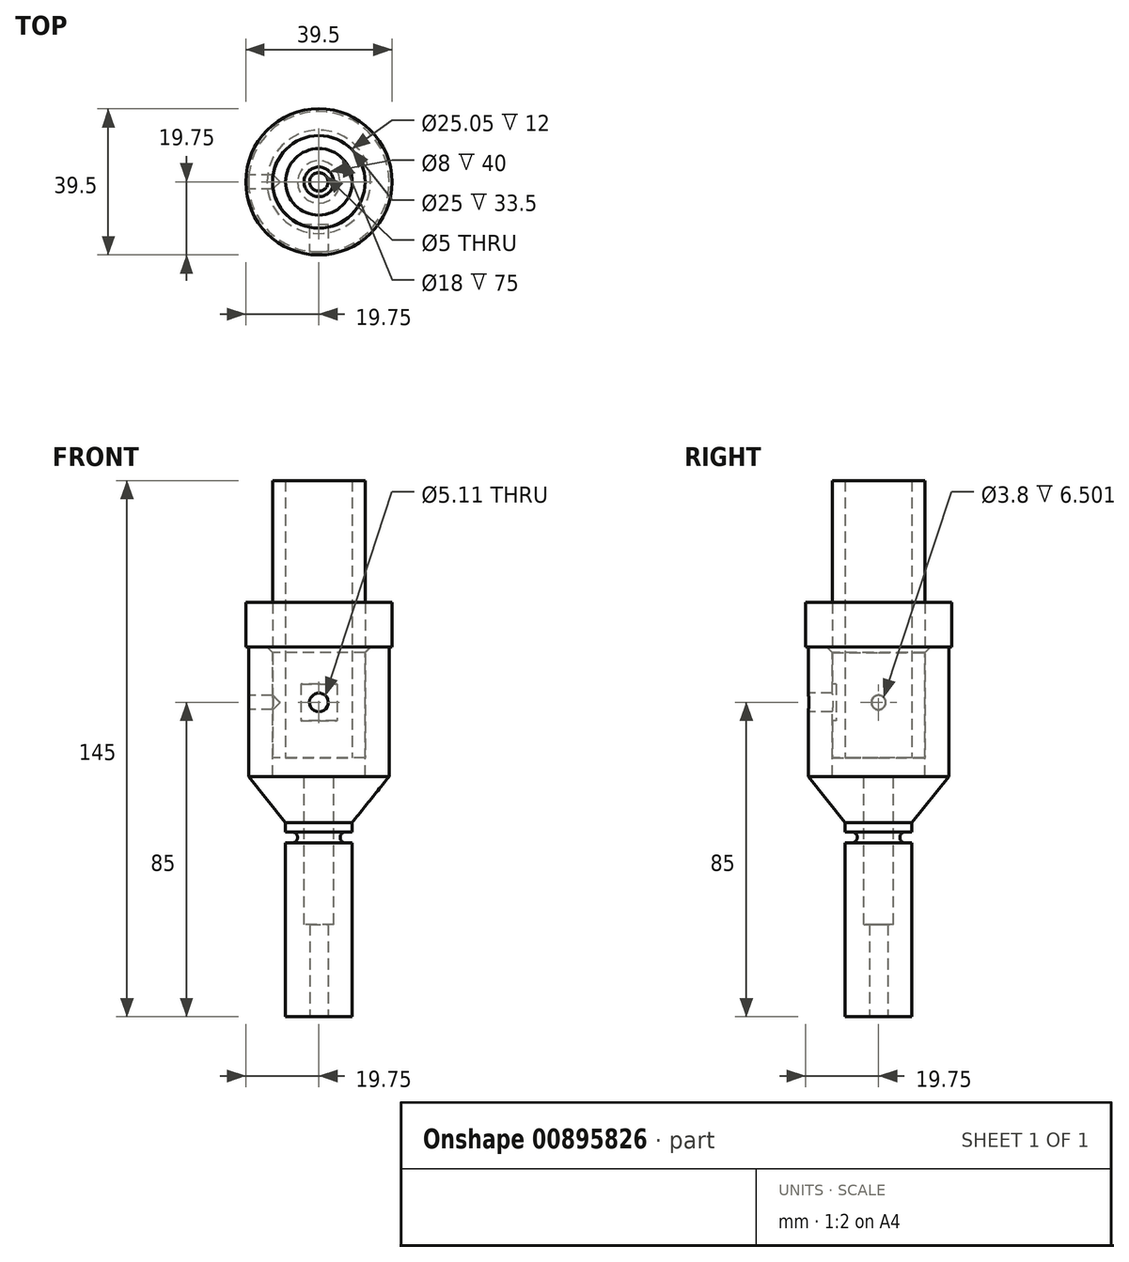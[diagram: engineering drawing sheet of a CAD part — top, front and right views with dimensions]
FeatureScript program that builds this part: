
annotation { "Feature Type Name" : "Feature", "Feature Type Description" : "" }
export const myFeature = defineFeature(function(context is Context, id is Id, definition is map)
    precondition{}
    {
        {
            var Q0;
            Q0=qCreatedBy(makeId("Top.planeOp"),FACE);
            var sketch = newSketch(context, id + "F0", { "sketchPlane" : qUnion([Q0])});
            skCircle(sketch, "E0", {"center": v(0, 0) * mm, "radius": 12.5 * mm});
            skSolve(sketch);
        }
        {
            var Q0;
            Q0=makeQuery(id+"F0.imprint","IMPRINT",FACE,{"disambiguationData":[TD([[makeQuery(id+"F0.imprint","IMPRINT",EDGE,{"derivedFrom":sQuery(id+"F0.wireOp",EDGE,"E0")}),1.0]])]});
            extrude(context, id + "F1", {"entities" : qUnion([Q0]), "depth" : 75 * mm, "offsetDistance" : 25.4 * mm});
        }
        {
            var Q0;
            Q0=qCreatedBy(makeId("Front.planeOp"),FACE);
            cPlane(context, id + "F2", {"entities" : qUnion([Q0]), "cplaneType" : CPlaneType.OFFSET, "offset" : 12.5 * mm, "width" : 150 * mm, "height" : 150 * mm});
        }
        {
            var Q0;
            Q0=qCreatedBy(id+"F2.planeOp",FACE);
            var sketch = newSketch(context, id + "F3", { "sketchPlane" : qUnion([Q0])});
            skLineSegment(sketch, "E1", {"start": v(12.5, 75) * mm, "end": v(12.5, 0) * mm});
            skLineSegment(sketch, "E2", {"start": v(-12.5, 0) * mm, "end": v(-12.5, 75) * mm});
            skLineSegment(sketch, "E3.0", {"start": v(-12.5, 0) * mm, "end": v(12.5, 0) * mm});
            skLineSegment(sketch, "E4.bottom", {"start": v(-12.5, 20) * mm, "end": v(12.5, 20) * mm});
            skLineSegment(sketch, "E4.top", {"start": v(-12.5, 10) * mm, "end": v(12.5, 10) * mm});
            skLineSegment(sketch, "E4.left", {"start": v(-12.5, 20) * mm, "end": v(-12.5, 10) * mm});
            skLineSegment(sketch, "E4.right", {"start": v(12.5, 20) * mm, "end": v(12.5, 10) * mm});
            skSolve(sketch);
        }
        {
            var Q0;
            Q0=makeQuery(id+"F3.imprint","IMPRINT",FACE,{"disambiguationData":[TD([[makeQuery(id+"F3.imprint","IMPRINT",EDGE,{"derivedFrom":sQuery(id+"F3.wireOp",EDGE,"E4.bottom")}),-1.0]])]});
            extrude(context, id + "F4", {"entities" : qUnion([Q0]), "operationType" : NewBodyOperationType.REMOVE, "oppositeDirection" : true, "depth" : 1 * mm, "offsetDistance" : 25 * mm});
        }
        {
            var Q0;
            Q0=qCreatedBy(makeId("Right.planeOp"),FACE);
            cPlane(context, id + "F5", {"entities" : qUnion([Q0]), "cplaneType" : CPlaneType.OFFSET, "offset" : 12.5 * mm, "oppositeDirection" : true, "width" : 150 * mm, "height" : 150 * mm});
        }
        {
            var Q0;
            Q0=qCreatedBy(id+"F5.planeOp",FACE);
            var sketch = newSketch(context, id + "F6", { "sketchPlane" : qUnion([Q0])});
            skLineSegment(sketch, "E5", {"start": v(0, 0) * mm, "end": v(0, 43.72) * mm, "construction": true});
            skPoint(sketch, "E6", {"position": v(0, 15) * mm});
            skSolve(sketch);
        }
        {
            var Q0;
            Q0=qCreatedBy(makeId("Top.planeOp"),FACE);
            var sketch = newSketch(context, id + "F7", { "sketchPlane" : qUnion([Q0])});
            skPoint(sketch, "E7", {"position": v(0, 0) * mm});
            skSolve(sketch);
        }
        {
            var Q0;
            Q0=sQuery(id+"F7.wireOp",VERTEX,"E7");
            var Q1;
            Q1=makeQuery(id+"F1.opExtrude","SWEPT_BODY",BODY,{"disambiguationData":[OSD([sQuery(id+"F0.wireOp",EDGE,"E0")])]});
            hole(context, id + "F8", {"style" : HoleStyle.SIMPLE, "endStyle" : HoleEndStyle.THROUGH, "oppositeDirection" : true, "holeDiameter" : 18 * mm, "majorDiameter" : 5 * mm, "isTappedThrough" : true, "tappedDepth" : 12 * mm, "tapClearance" : 3, "startFromSketch" : true, "locations" : qUnion([Q0]), "scope" : qUnion([Q1])});
        }
        {
            var Q0;
            Q0=qCreatedBy(makeId("Top.planeOp"),FACE);
            cPlane(context, id + "F9", {"entities" : qUnion([Q0]), "cplaneType" : CPlaneType.OFFSET, "offset" : 30 * mm, "width" : 150 * mm, "height" : 150 * mm});
        }
        {
            var Q0;
            Q0=qCreatedBy(id+"F9.planeOp",FACE);
            var sketch = newSketch(context, id + "F10", { "sketchPlane" : qUnion([Q0])});
            skCircle(sketch, "E8", {"center": v(0, 0) * mm, "radius": 12.53 * mm});
            skCircle(sketch, "E9", {"center": v(0, 0) * mm, "radius": 19.75 * mm});
            skSolve(sketch);
        }
        {
            var Q0;
            Q0=makeQuery(id+"F10.imprint","IMPRINT",FACE,{"disambiguationData":[TD([[makeQuery(id+"F10.imprint","IMPRINT",EDGE,{"derivedFrom":sQuery(id+"F10.wireOp",EDGE,"E8")}),-1.0]])]});
            extrude(context, id + "F11", {"entities" : qUnion([Q0]), "depth" : 12 * mm, "offsetDistance" : 25 * mm});
        }
        {
            var Q0;
            Q0=qCreatedBy(makeId("Front.planeOp"),FACE);
            var sketch = newSketch(context, id + "F12", { "sketchPlane" : qUnion([Q0])});
            skLineSegment(sketch, "E10", {"start": v(12.5, 30) * mm, "end": v(19, 30) * mm});
            skLineSegment(sketch, "E11", {"start": v(19, 30) * mm, "end": v(19, -5) * mm});
            skLineSegment(sketch, "E12", {"start": v(19, -5) * mm, "end": v(9, -17.5) * mm});
            skLineSegment(sketch, "E13", {"start": v(4, -70) * mm, "end": v(4, -5) * mm});
            skLineSegment(sketch, "E14", {"start": v(4, -5) * mm, "end": v(12.5, -5) * mm});
            skLineSegment(sketch, "E15", {"start": v(12.5, -5) * mm, "end": v(12.5, 30) * mm});
            skLineSegment(sketch, "E16", {"start": v(9, -17.5) * mm, "end": v(9, -70) * mm});
            skLineSegment(sketch, "E17", {"start": v(9, -70) * mm, "end": v(4, -70) * mm});
            skLineSegment(sketch, "E18", {"start": v(0, 0) * mm, "end": v(0, -44.4) * mm, "construction": true});
            skSolve(sketch);
        }
        {
            var Q0;
            Q0=makeQuery(id+"F12.imprint","IMPRINT",FACE,{"disambiguationData":[TD([[makeQuery(id+"F12.imprint","IMPRINT",EDGE,{"derivedFrom":sQuery(id+"F12.wireOp",EDGE,"E10")}),-1.0]])]});
            var Q1;
            Q1 = qConstructionFilter(qBodyType(qCreatedBy(id + "F12" ,EDGE), BodyType.WIRE), ConstructionObject.NO);
            var Q2;
            Q2=sQuery(id+"F12.wireOp",EDGE,"E18");
            revolve(context, id + "F13", {"surfaceOperationType" : NewSurfaceOperationType.NEW, "entities" : qUnion([Q0]), "surfaceEntities" : qUnion([Q1]), "axis" : qUnion([Q2]), "revolveType" : RevolveType.FULL});
        }
        {
            var Q0;
            Q0=qCreatedBy(makeId("Top.planeOp"),FACE);
            cPlane(context, id + "F14", {"entities" : qUnion([Q0]), "cplaneType" : CPlaneType.OFFSET, "offset" : 15 * mm, "width" : 150 * mm, "height" : 150 * mm});
        }
        {
            var Q0;
            Q0=qCreatedBy(id+"F14.planeOp",FACE);
            var sketch = newSketch(context, id + "F15", { "sketchPlane" : qUnion([Q0])});
            skCircle(sketch, "E19.0", {"center": v(0, 0) * mm, "radius": 12.5 * mm, "construction": true});
            skLineSegment(sketch, "E20", {"start": v(-12.5, -2) * mm, "end": v(-10.5, 0) * mm, "construction": true});
            skLineSegment(sketch, "E21", {"start": v(-10.5, 0) * mm, "end": v(-12.5, 2) * mm, "construction": true});
            skLineSegment(sketch, "E22", {"start": v(-12.5, 2) * mm, "end": v(-12.5, -2) * mm, "construction": true});
            skPoint(sketch, "E23", {"position": v(-12.5, 0) * mm});
            skLineSegment(sketch, "E24", {"start": v(-12.5, 0) * mm, "end": v(-12.5, -2) * mm});
            skLineSegment(sketch, "E25", {"start": v(-10.5, 0) * mm, "end": v(-12.5, -2) * mm});
            skLineSegment(sketch, "E26", {"start": v(-10.5, 0) * mm, "end": v(-12.5, 0) * mm});
            skSolve(sketch);
        }
        {
            var Q0;
            Q0=makeQuery(id+"F15.imprint","IMPRINT",FACE,{"disambiguationData":[TD([[makeQuery(id+"F15.imprint","IMPRINT",EDGE,{"derivedFrom":sQuery(id+"F15.wireOp",EDGE,"E24")}),1.0]])]});
            var Q1;
            Q1 = qConstructionFilter(qBodyType(qCreatedBy(id + "F15" ,EDGE), BodyType.WIRE), ConstructionObject.NO);
            var Q2;
            Q2=sQuery(id+"F15.wireOp",EDGE,"E26");
            revolve(context, id + "F16", {"operationType" : NewBodyOperationType.REMOVE, "surfaceOperationType" : NewSurfaceOperationType.NEW, "entities" : qUnion([Q0]), "surfaceEntities" : qUnion([Q1]), "axis" : qUnion([Q2]), "revolveType" : RevolveType.FULL, "oppositeDirection" : true});
        }
        {
            var Q0;
            Q0=qCreatedBy(makeId("Front.planeOp"),FACE);
            cPlane(context, id + "F17", {"entities" : qUnion([Q0]), "cplaneType" : CPlaneType.OFFSET, "offset" : 19 * mm, "width" : 150 * mm, "height" : 150 * mm});
        }
        {
            var Q0;
            Q0=qCreatedBy(id+"F17.planeOp",FACE);
            var sketch = newSketch(context, id + "F18", { "sketchPlane" : qUnion([Q0])});
            skPoint(sketch, "E27", {"position": v(0, 15) * mm});
            skSolve(sketch);
        }
        {
            var Q0;
            Q0=sQuery(id+"F18.wireOp",VERTEX,"E27");
            var Q1;
            Q1=makeQuery(id+"F13.opRevolve","SWEPT_BODY",BODY,{"disambiguationData":[OSD([sQuery(id+"F12.wireOp",EDGE,"E10"),sQuery(id+"F12.wireOp",EDGE,"E11"),sQuery(id+"F12.wireOp",EDGE,"E12"),sQuery(id+"F12.wireOp",EDGE,"E13"),sQuery(id+"F12.wireOp",EDGE,"E14"),sQuery(id+"F12.wireOp",EDGE,"E15"),sQuery(id+"F12.wireOp",EDGE,"E16"),sQuery(id+"F12.wireOp",EDGE,"E17")])]});
            hole(context, id + "F19", {"style" : HoleStyle.SIMPLE, "endStyle" : HoleEndStyle.BLIND, "standardTappedOrClearance" : lookupTablePath({ "standard" : "ANSI", "engagement" : "75%", "pitch" : "20 tpi", "size" : "1/4", "type" : "Tapped" }), "standardBlindInLast" : lookupTablePath({ "standard" : "ANSI", "engagement" : "75%", "pitch" : "20 tpi", "size" : "1/4", "type" : "Tapped" }), "holeDiameter" : 5.1 * mm, "majorDiameter" : 6.35 * mm, "showTappedDepth" : true, "holeDepth" : 10.8 * mm, "isTappedThrough" : true, "tappedDepth" : 7 * mm, "tapClearance" : 3, "startFromSketch" : true, "locations" : qUnion([Q0]), "scope" : qUnion([Q1])});
        }
        {
            var Q0;
            Q0=qCreatedBy(makeId("Right.planeOp"),FACE);
            cPlane(context, id + "F20", {"entities" : qUnion([Q0]), "cplaneType" : CPlaneType.OFFSET, "offset" : 19 * mm, "oppositeDirection" : true, "width" : 150 * mm, "height" : 150 * mm});
        }
        {
            var Q0;
            Q0=qCreatedBy(id+"F20.planeOp",FACE);
            var sketch = newSketch(context, id + "F21", { "sketchPlane" : qUnion([Q0])});
            skPoint(sketch, "E28", {"position": v(0, 15) * mm});
            skSolve(sketch);
        }
        {
            var Q0;
            Q0=sQuery(id+"F21.wireOp",VERTEX,"E28");
            var Q1;
            Q1=makeQuery(id+"F13.opRevolve","SWEPT_BODY",BODY,{"disambiguationData":[OSD([sQuery(id+"F12.wireOp",EDGE,"E10"),sQuery(id+"F12.wireOp",EDGE,"E11"),sQuery(id+"F12.wireOp",EDGE,"E12"),sQuery(id+"F12.wireOp",EDGE,"E13"),sQuery(id+"F12.wireOp",EDGE,"E14"),sQuery(id+"F12.wireOp",EDGE,"E15"),sQuery(id+"F12.wireOp",EDGE,"E16"),sQuery(id+"F12.wireOp",EDGE,"E17")])]});
            hole(context, id + "F22", {"style" : HoleStyle.SIMPLE, "endStyle" : HoleEndStyle.BLIND, "oppositeDirection" : true, "standardTappedOrClearance" : lookupTablePath({ "standard" : "ANSI", "engagement" : "75%", "pitch" : "24 tpi", "size" : "#10", "type" : "Tapped" }), "standardBlindInLast" : lookupTablePath({ "standard" : "ANSI", "engagement" : "75%", "pitch" : "24 tpi", "size" : "#10", "type" : "Tapped" }), "holeDiameter" : 3.8 * mm, "majorDiameter" : 4.83 * mm, "showTappedDepth" : true, "holeDepth" : 10.17 * mm, "isTappedThrough" : true, "tappedDepth" : 7 * mm, "tapClearance" : 3, "startFromSketch" : true, "locations" : qUnion([Q0]), "scope" : qUnion([Q1])});
        }
        {
            var Q0;
            Q0=makeQuery(id+"F13.opRevolve","SWEPT_EDGE",EDGE,{"disambiguationData":[OSD([sQuery(id+"F12.wireOp",EDGE,"E10"),sQuery(id+"F12.wireOp",EDGE,"E15")])]});
            chamfer(context, id + "F23", {"entities" : qUnion([Q0]), "width" : 1.5 * mm, "tangentPropagation" : true});
        }
        {
            var Q0;
            Q0=makeQuery(id+"F13.opRevolve","SWEPT_FACE",FACE,{"disambiguationData":[OSD([sQuery(id+"F12.wireOp",EDGE,"E17")])]});
            var sketch = newSketch(context, id + "F24", { "sketchPlane" : qUnion([Q0])});
            skCircle(sketch, "E29.0", {"center": v(0, 0) * mm, "radius": 4 * mm});
            skCircle(sketch, "E30", {"center": v(0, 0) * mm, "radius": 2.5 * mm});
            skSolve(sketch);
        }
        {
            var Q0;
            Q0=makeQuery(id+"F24.imprint","IMPRINT",FACE,{"disambiguationData":[TD([[makeQuery(id+"F24.imprint","IMPRINT",EDGE,{"derivedFrom":sQuery(id+"F24.wireOp",EDGE,"E29.0")}),-1.0]])]});
            extrude(context, id + "F25", {"entities" : qUnion([Q0]), "operationType" : NewBodyOperationType.ADD, "oppositeDirection" : true, "depth" : 25 * mm, "offsetDistance" : 25 * mm});
        }
        {
            var Q0;
            Q0=makeQuery(id+"F25.boolean.opBoolean","MERGE",FACE,{"derivedFrom":[makeQuery(id+"F13.opRevolve","SWEPT_FACE",FACE,{"disambiguationData":[OSD([sQuery(id+"F12.wireOp",EDGE,"E17")])]}),makeQuery(id+"F25.opExtrude","CAP_FACE",FACE,{"disambiguationData":[OSD([sQuery(id+"F24.wireOp",EDGE,"E29.0"),sQuery(id+"F24.wireOp",EDGE,"E30")])],"isStart":true})]});
            cPlane(context, id + "F26", {"entities" : qUnion([Q0]), "cplaneType" : CPlaneType.OFFSET, "offset" : 50 * mm, "oppositeDirection" : true, "width" : 150 * mm, "height" : 150 * mm});
        }
        {
            var Q0;
            Q0=qCreatedBy(id+"F26.planeOp",FACE);
            var sketch = newSketch(context, id + "F27", { "sketchPlane" : qUnion([Q0])});
            skCircle(sketch, "E31.0", {"center": v(0, 0) * mm, "radius": 9 * mm});
            skCircle(sketch, "E32", {"center": v(0, 0) * mm, "radius": 5.75 * mm});
            skSolve(sketch);
        }
        {
            var Q0;
            Q0=makeQuery(id+"F27.imprint","IMPRINT",FACE,{"disambiguationData":[TD([[makeQuery(id+"F27.imprint","IMPRINT",EDGE,{"derivedFrom":sQuery(id+"F27.wireOp",EDGE,"E31.0")}),1.0]])]});
            extrude(context, id + "F28", {"entities" : qUnion([Q0]), "operationType" : NewBodyOperationType.REMOVE, "depth" : 3 * mm, "offsetDistance" : 25 * mm});
        }
        {
            var Q0;
            Q0=makeQuery(id+"F28.boolean.opBoolean","COPY",EDGE,{"derivedFrom":makeQuery(id+"F28.opExtrude","CAP_EDGE",EDGE,{"disambiguationData":[OSD([sQuery(id+"F27.wireOp",EDGE,"E32")])],"isStart":false})});
            var Q1;
            Q1=makeQuery(id+"F28.boolean.opBoolean","COPY",EDGE,{"derivedFrom":makeQuery(id+"F28.opExtrude","CAP_EDGE",EDGE,{"disambiguationData":[OSD([sQuery(id+"F27.wireOp",EDGE,"E32")])],"isStart":true})});
            fillet(context, id + "F29", {"entities" : qUnion([Q0, Q1]), "radius" : 1.5 * mm, "tangentPropagation" : true, "allowEdgeOverflow" : false});
        }
    });
